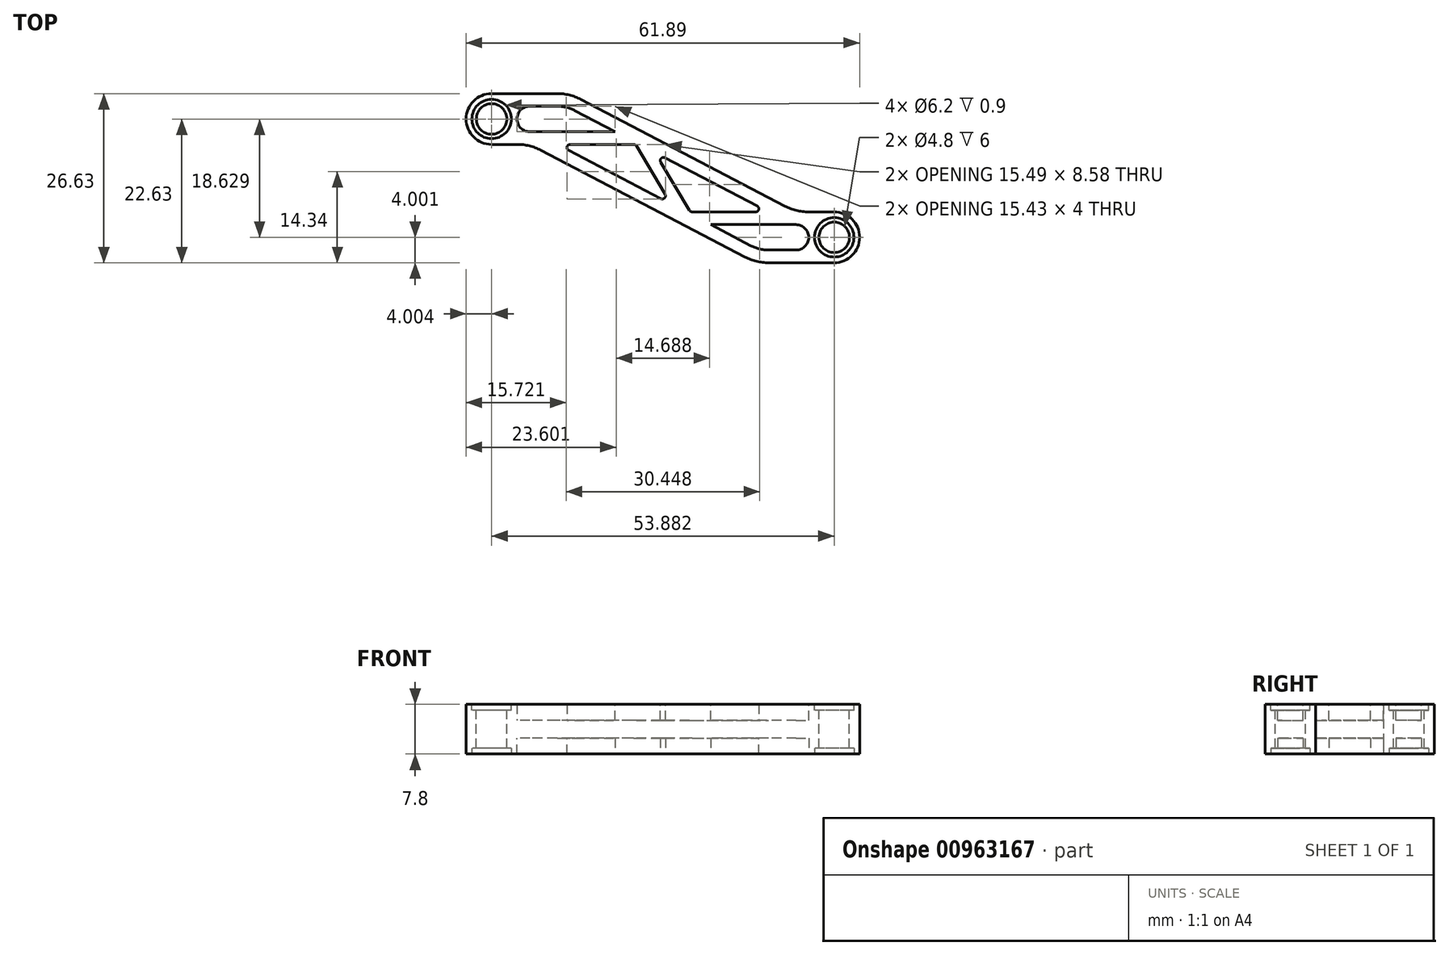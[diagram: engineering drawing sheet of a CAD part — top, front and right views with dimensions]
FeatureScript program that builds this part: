
annotation { "Feature Type Name" : "Feature", "Feature Type Description" : "" }
export const myFeature = defineFeature(function(context is Context, id is Id, definition is map)
    precondition{}
    {
        {
            var Q0;
            Q0=qCreatedBy(makeId("Top.planeOp"),FACE);
            var sketch = newSketch(context, id + "F0", { "sketchPlane" : qUnion([Q0])});
            skLineSegment(sketch, "E0", {"start": v(-26.52, 8) * mm, "end": v(-10.24, 8) * mm});
            skLineSegment(sketch, "E1", {"start": v(-10.24, 8) * mm, "end": v(25.37, -10.63) * mm});
            skLineSegment(sketch, "E2", {"start": v(25.37, -10.63) * mm, "end": v(35.37, -10.63) * mm});
            skLineSegment(sketch, "E3", {"start": v(35.37, -10.63) * mm, "end": v(35.37, -18.63) * mm});
            skLineSegment(sketch, "E4", {"start": v(35.37, -18.63) * mm, "end": v(19.09, -18.63) * mm});
            skLineSegment(sketch, "E5", {"start": v(19.09, -18.63) * mm, "end": v(-16.52, 0) * mm});
            skLineSegment(sketch, "E6", {"start": v(-16.52, 0) * mm, "end": v(-26.52, 0) * mm});
            skLineSegment(sketch, "E7", {"start": v(-26.52, 0) * mm, "end": v(-26.52, 8) * mm});
            skSolve(sketch);
        }
        {
            var Q0;
            Q0 = qSketchRegion(id + "F0", true);
            extrude(context, id + "F1", {"entities" : qUnion([Q0]), "depth" : 3.9 * mm, "offsetDistance" : 25 * mm});
        }
        {
            var Q0;
            Q0=makeQuery(id+"F1.opExtrude","CAP_FACE",FACE,{"disambiguationData":[OSD([sQuery(id+"F0.wireOp",EDGE,"E0"),sQuery(id+"F0.wireOp",EDGE,"E1"),sQuery(id+"F0.wireOp",EDGE,"E2"),sQuery(id+"F0.wireOp",EDGE,"E3"),sQuery(id+"F0.wireOp",EDGE,"E4"),sQuery(id+"F0.wireOp",EDGE,"E5"),sQuery(id+"F0.wireOp",EDGE,"E6"),sQuery(id+"F0.wireOp",EDGE,"E7")])],"isStart":false});
            var sketch = newSketch(context, id + "F2", { "sketchPlane" : qUnion([Q0])});
            skLineSegment(sketch, "E8", {"start": v(-10.73, 6) * mm, "end": v(24.87, -12.63) * mm});
            skLineSegment(sketch, "E9", {"start": v(19.58, -16.63) * mm, "end": v(-16.02, 2) * mm});
            skLineSegment(sketch, "E10", {"start": v(19.09, -18.63) * mm, "end": v(25.37, -10.63) * mm, "construction": true});
            skLineSegment(sketch, "E11", {"start": v(-16.52, 0) * mm, "end": v(-10.24, 8) * mm, "construction": true});
            skLineSegment(sketch, "E12.bottom", {"start": v(27.37, -16.63) * mm, "end": v(19.58, -16.63) * mm});
            skLineSegment(sketch, "E12.top", {"start": v(27.37, -12.63) * mm, "end": v(24.87, -12.63) * mm});
            skLineSegment(sketch, "E12.left", {"start": v(27.37, -16.63) * mm, "end": v(27.37, -12.63) * mm});
            skLineSegment(sketch, "E13.bottom", {"start": v(-16.02, 2) * mm, "end": v(-18.52, 2) * mm});
            skLineSegment(sketch, "E13.top", {"start": v(-10.73, 6) * mm, "end": v(-18.52, 6) * mm});
            skLineSegment(sketch, "E13.right", {"start": v(-18.52, 2) * mm, "end": v(-18.52, 6) * mm});
            skSolve(sketch);
        }
        {
            var Q0;
            Q0=makeQuery(id+"F2.imprint","IMPRINT",FACE,{"disambiguationData":[TD([[makeQuery(id+"F2.imprint","IMPRINT",EDGE,{"derivedFrom":sQuery(id+"F2.wireOp",EDGE,"E8")}),-1.0]])]});
            extrude(context, id + "F3", {"entities" : qUnion([Q0]), "operationType" : NewBodyOperationType.REMOVE, "oppositeDirection" : true, "depth" : (4 - 1.5) * mm, "offsetDistance" : 25 * mm});
        }
        {
            var Q0;
            Q0=makeQuery(id+"F1.opExtrude","CAP_FACE",FACE,{"disambiguationData":[OSD([sQuery(id+"F0.wireOp",EDGE,"E0"),sQuery(id+"F0.wireOp",EDGE,"E1"),sQuery(id+"F0.wireOp",EDGE,"E2"),sQuery(id+"F0.wireOp",EDGE,"E3"),sQuery(id+"F0.wireOp",EDGE,"E4"),sQuery(id+"F0.wireOp",EDGE,"E5"),sQuery(id+"F0.wireOp",EDGE,"E6"),sQuery(id+"F0.wireOp",EDGE,"E7")])],"isStart":false});
            var sketch = newSketch(context, id + "F4", { "sketchPlane" : qUnion([Q0])});
            skLineSegment(sketch, "E14", {"start": v(24.87, -12.63) * mm, "end": v(11.93, -12.63) * mm});
            skLineSegment(sketch, "E15", {"start": v(-16.02, 2) * mm, "end": v(-3.08, 2) * mm});
            skLineSegment(sketch, "E16", {"start": v(21.05, -10.63) * mm, "end": v(8.76, -10.63) * mm});
            skLineSegment(sketch, "E17", {"start": v(-12.2, 0) * mm, "end": v(0.74, 0) * mm});
            skLineSegment(sketch, "E18", {"start": v(5.67, -9.35) * mm, "end": v(-0.2, 0.5) * mm});
            skLineSegment(sketch, "E19", {"start": v(11.93, -12.63) * mm, "end": v(5.67, -9.35) * mm});
            skLineSegment(sketch, "E20", {"start": v(-3.08, 2) * mm, "end": v(3.19, -1.28) * mm});
            skLineSegment(sketch, "E21", {"start": v(-12.2, 0) * mm, "end": v(-16.02, 2) * mm});
            skLineSegment(sketch, "E22", {"start": v(24.87, -12.63) * mm, "end": v(21.05, -10.63) * mm});
            skLineSegment(sketch, "E23.trimOffspring", {"start": v(3.19, -1.28) * mm, "end": v(8.76, -10.63) * mm});
            skSolve(sketch);
        }
        {
            var Q0;
            Q0=makeQuery(id+"F4.imprint","IMPRINT",FACE,{"disambiguationData":[TD([[makeQuery(id+"F4.imprint","IMPRINT",EDGE,{"derivedFrom":sQuery(id+"F4.wireOp",EDGE,"E14")}),-1.0]])]});
            var Q1;
            {var subQ1=sQuery(id+"F4.wireOp",EDGE,"E15");Q1=makeQuery(id+"F4.imprint","IMPRINT",FACE,{"disambiguationData":[TD([[makeQuery(id+"F4.imprint","IMPRINT",EDGE,{"derivedFrom":subQ1}),-1.0]])]});}
            var Q2;
            {var subQ0=sQuery(id+"F4.wireOp",EDGE,"E20");var subQ1=sQuery(id+"F4.wireOp",EDGE,"E17");var subQ2=makeQuery(id+"F4.imprint","INTERSECT",VERTEX,{"derivedFrom":[subQ1,subQ0]});Q2=makeQuery(id+"F4.imprint","IMPRINT",FACE,{"disambiguationData":[TD([[makeQuery(id+"F4.imprint","IMPRINT",EDGE,{"disambiguationData":[TD([[subQ2,1.0]])],"derivedFrom":subQ1}),1.0]])]});}
            var Q3;
            Q3=makeQuery(id+"F3.boolean.opBoolean","COPY",FACE,{"derivedFrom":makeQuery(id+"F3.opExtrude","CAP_FACE",FACE,{"disambiguationData":[OSD([sQuery(id+"F2.wireOp",EDGE,"E8"),sQuery(id+"F2.wireOp",EDGE,"E9"),sQuery(id+"F2.wireOp",EDGE,"E12.bottom"),sQuery(id+"F2.wireOp",EDGE,"E12.top"),sQuery(id+"F2.wireOp",EDGE,"E12.left"),sQuery(id+"F2.wireOp",EDGE,"E13.bottom"),sQuery(id+"F2.wireOp",EDGE,"E13.top"),sQuery(id+"F2.wireOp",EDGE,"E13.right")])],"isStart":false})});
            extrude(context, id + "F5", {"entities" : qUnion([Q0, Q1, Q2]), "operationType" : NewBodyOperationType.ADD, "endBound" : BoundingType.UP_TO_SURFACE, "oppositeDirection" : true, "depth" : 25 * mm, "endBoundEntityFace" : qUnion([Q3]), "offsetDistance" : 25 * mm});
        }
        {
            var Q0;
            Q0=makeQuery(id+"F1.opExtrude","SWEPT_EDGE",EDGE,{"disambiguationData":[OSD([sQuery(id+"F0.wireOp",EDGE,"E0"),sQuery(id+"F0.wireOp",EDGE,"E1")])]});
            var Q1;
            Q1=makeQuery(id+"F1.opExtrude","SWEPT_EDGE",EDGE,{"disambiguationData":[OSD([sQuery(id+"F0.wireOp",EDGE,"E1"),sQuery(id+"F0.wireOp",EDGE,"E2")])]});
            var Q2;
            Q2=makeQuery(id+"F1.opExtrude","SWEPT_EDGE",EDGE,{"disambiguationData":[OSD([sQuery(id+"F0.wireOp",EDGE,"E4"),sQuery(id+"F0.wireOp",EDGE,"E5")])]});
            var Q3;
            Q3=makeQuery(id+"F1.opExtrude","SWEPT_EDGE",EDGE,{"disambiguationData":[OSD([sQuery(id+"F0.wireOp",EDGE,"E5"),sQuery(id+"F0.wireOp",EDGE,"E6")])]});
            fillet(context, id + "F6", {"entities" : qUnion([Q0, Q1, Q2, Q3]), "radius" : 8 * mm, "tangentPropagation" : true, "allowEdgeOverflow" : false});
        }
        {
            var Q0;
            Q0=makeQuery(id+"F1.opExtrude","SWEPT_EDGE",EDGE,{"disambiguationData":[OSD([sQuery(id+"F0.wireOp",EDGE,"E0"),sQuery(id+"F0.wireOp",EDGE,"E7")])]});
            var Q1;
            Q1=makeQuery(id+"F1.opExtrude","SWEPT_EDGE",EDGE,{"disambiguationData":[OSD([sQuery(id+"F0.wireOp",EDGE,"E6"),sQuery(id+"F0.wireOp",EDGE,"E7")])]});
            var Q2;
            Q2=makeQuery(id+"F1.opExtrude","SWEPT_EDGE",EDGE,{"disambiguationData":[OSD([sQuery(id+"F0.wireOp",EDGE,"E2"),sQuery(id+"F0.wireOp",EDGE,"E3")])]});
            var Q3;
            Q3=makeQuery(id+"F1.opExtrude","SWEPT_EDGE",EDGE,{"disambiguationData":[OSD([sQuery(id+"F0.wireOp",EDGE,"E3"),sQuery(id+"F0.wireOp",EDGE,"E4")])]});
            fillet(context, id + "F7", {"entities" : qUnion([Q0, Q1, Q2, Q3]), "radius" : 4 * mm, "tangentPropagation" : true, "allowEdgeOverflow" : false});
        }
        {
            var Q0;
            Q0=makeQuery(id+"F1.opExtrude","CAP_FACE",FACE,{"disambiguationData":[OSD([sQuery(id+"F0.wireOp",EDGE,"E0"),sQuery(id+"F0.wireOp",EDGE,"E1"),sQuery(id+"F0.wireOp",EDGE,"E2"),sQuery(id+"F0.wireOp",EDGE,"E3"),sQuery(id+"F0.wireOp",EDGE,"E4"),sQuery(id+"F0.wireOp",EDGE,"E5"),sQuery(id+"F0.wireOp",EDGE,"E6"),sQuery(id+"F0.wireOp",EDGE,"E7")])],"isStart":false});
            var sketch = newSketch(context, id + "F8", { "sketchPlane" : qUnion([Q0])});
            skCircle(sketch, "E24", {"center": v(-22.52, 4) * mm, "radius": 3.1 * mm});
            skCircle(sketch, "E25", {"center": v(-22.52, 4) * mm, "radius": 2.4 * mm});
            skCircle(sketch, "E26", {"center": v(31.37, -14.63) * mm, "radius": 3.1 * mm});
            skCircle(sketch, "E27", {"center": v(31.37, -14.63) * mm, "radius": 2.4 * mm});
            skSolve(sketch);
        }
        {
            var Q0;
            Q0=makeQuery(id+"F8.imprint","IMPRINT",FACE,{"disambiguationData":[TD([[makeQuery(id+"F8.imprint","IMPRINT",EDGE,{"derivedFrom":sQuery(id+"F8.wireOp",EDGE,"E25")}),1.0]])]});
            var Q1;
            Q1=makeQuery(id+"F8.imprint","IMPRINT",FACE,{"disambiguationData":[TD([[makeQuery(id+"F8.imprint","IMPRINT",EDGE,{"derivedFrom":sQuery(id+"F8.wireOp",EDGE,"E27")}),1.0]])]});
            extrude(context, id + "F9", {"entities" : qUnion([Q0, Q1]), "operationType" : NewBodyOperationType.REMOVE, "endBound" : BoundingType.THROUGH_ALL, "oppositeDirection" : true, "depth" : 25 * mm, "offsetDistance" : 25 * mm});
        }
        {
            var Q0;
            Q0=makeQuery(id+"F8.imprint","IMPRINT",FACE,{"disambiguationData":[TD([[makeQuery(id+"F8.imprint","IMPRINT",EDGE,{"derivedFrom":sQuery(id+"F8.wireOp",EDGE,"E24")}),1.0]])]});
            var Q1;
            Q1=makeQuery(id+"F8.imprint","IMPRINT",FACE,{"disambiguationData":[TD([[makeQuery(id+"F8.imprint","IMPRINT",EDGE,{"derivedFrom":sQuery(id+"F8.wireOp",EDGE,"E26")}),1.0]])]});
            extrude(context, id + "F10", {"entities" : qUnion([Q0, Q1]), "operationType" : NewBodyOperationType.REMOVE, "oppositeDirection" : true, "depth" : .9 * mm, "offsetDistance" : 25 * mm});
        }
        {
            var Q0;
            Q0=makeQuery(id+"F1.opExtrude","SWEPT_BODY",BODY,{"disambiguationData":[OSD([sQuery(id+"F0.wireOp",EDGE,"E0"),sQuery(id+"F0.wireOp",EDGE,"E1"),sQuery(id+"F0.wireOp",EDGE,"E2"),sQuery(id+"F0.wireOp",EDGE,"E3"),sQuery(id+"F0.wireOp",EDGE,"E4"),sQuery(id+"F0.wireOp",EDGE,"E5"),sQuery(id+"F0.wireOp",EDGE,"E6"),sQuery(id+"F0.wireOp",EDGE,"E7")])]});
            var Q1;
            Q1=makeQuery(id+"F1.opExtrude","CAP_FACE",FACE,{"disambiguationData":[OSD([sQuery(id+"F0.wireOp",EDGE,"E0"),sQuery(id+"F0.wireOp",EDGE,"E1"),sQuery(id+"F0.wireOp",EDGE,"E2"),sQuery(id+"F0.wireOp",EDGE,"E3"),sQuery(id+"F0.wireOp",EDGE,"E4"),sQuery(id+"F0.wireOp",EDGE,"E5"),sQuery(id+"F0.wireOp",EDGE,"E6"),sQuery(id+"F0.wireOp",EDGE,"E7")])],"isStart":true});
            mirror(context, id + "F11", {"operationType" : NewBodyOperationType.ADD, "entities" : qUnion([Q0]), "mirrorPlane" : qUnion([Q1])});
        }
        {
            var Q0;
            Q0=makeQuery(id+"F3.boolean.opBoolean","COPY",EDGE,{"derivedFrom":makeQuery(id+"F3.opExtrude","SWEPT_EDGE",EDGE,{"disambiguationData":[OSD([sQuery(id+"F2.wireOp",EDGE,"E12.bottom"),sQuery(id+"F2.wireOp",EDGE,"E12.left")])]})});
            var Q1;
            Q1=makeQuery(id+"F3.boolean.opBoolean","COPY",EDGE,{"derivedFrom":makeQuery(id+"F3.opExtrude","SWEPT_EDGE",EDGE,{"disambiguationData":[OSD([sQuery(id+"F2.wireOp",EDGE,"E12.top"),sQuery(id+"F2.wireOp",EDGE,"E12.left")])]})});
            var Q2;
            Q2=makeQuery(id+"F3.boolean.opBoolean","COPY",EDGE,{"derivedFrom":makeQuery(id+"F3.opExtrude","SWEPT_EDGE",EDGE,{"disambiguationData":[OSD([sQuery(id+"F2.wireOp",EDGE,"E13.bottom"),sQuery(id+"F2.wireOp",EDGE,"E13.right")])]})});
            var Q3;
            Q3=makeQuery(id+"F3.boolean.opBoolean","COPY",EDGE,{"derivedFrom":makeQuery(id+"F3.opExtrude","SWEPT_EDGE",EDGE,{"disambiguationData":[OSD([sQuery(id+"F2.wireOp",EDGE,"E13.top"),sQuery(id+"F2.wireOp",EDGE,"E13.right")])]})});
            var Q4;
            Q4=makeQuery(id+"F11.opPattern","COPY",EDGE,{"derivedFrom":makeQuery(id+"F3.boolean.opBoolean","COPY",EDGE,{"derivedFrom":makeQuery(id+"F3.opExtrude","SWEPT_EDGE",EDGE,{"disambiguationData":[OSD([sQuery(id+"F2.wireOp",EDGE,"E13.bottom"),sQuery(id+"F2.wireOp",EDGE,"E13.right")])]})}),"instanceName":"1"});
            var Q5;
            Q5=makeQuery(id+"F11.opPattern","COPY",EDGE,{"derivedFrom":makeQuery(id+"F3.boolean.opBoolean","COPY",EDGE,{"derivedFrom":makeQuery(id+"F3.opExtrude","SWEPT_EDGE",EDGE,{"disambiguationData":[OSD([sQuery(id+"F2.wireOp",EDGE,"E13.top"),sQuery(id+"F2.wireOp",EDGE,"E13.right")])]})}),"instanceName":"1"});
            var Q6;
            Q6=makeQuery(id+"F11.opPattern","COPY",EDGE,{"derivedFrom":makeQuery(id+"F3.boolean.opBoolean","COPY",EDGE,{"derivedFrom":makeQuery(id+"F3.opExtrude","SWEPT_EDGE",EDGE,{"disambiguationData":[OSD([sQuery(id+"F2.wireOp",EDGE,"E12.bottom"),sQuery(id+"F2.wireOp",EDGE,"E12.left")])]})}),"instanceName":"1"});
            var Q7;
            Q7=makeQuery(id+"F11.opPattern","COPY",EDGE,{"derivedFrom":makeQuery(id+"F3.boolean.opBoolean","COPY",EDGE,{"derivedFrom":makeQuery(id+"F3.opExtrude","SWEPT_EDGE",EDGE,{"disambiguationData":[OSD([sQuery(id+"F2.wireOp",EDGE,"E12.top"),sQuery(id+"F2.wireOp",EDGE,"E12.left")])]})}),"instanceName":"1"});
            fillet(context, id + "F12", {"entities" : qUnion([Q0, Q1, Q2, Q3, Q4, Q5, Q6, Q7]), "radius" : 2 * mm, "tangentPropagation" : true, "allowEdgeOverflow" : false});
        }
        {
            var Q0;
            Q0=makeQuery(id+"F11.opPattern","COPY",EDGE,{"derivedFrom":makeQuery(id+"F3.boolean.opBoolean","COPY",EDGE,{"derivedFrom":makeQuery(id+"F3.opExtrude","SWEPT_EDGE",EDGE,{"disambiguationData":[OSD([sQuery(id+"F2.wireOp",EDGE,"E9"),sQuery(id+"F2.wireOp",EDGE,"E12.bottom")])]})}),"instanceName":"1"});
            var Q1;
            Q1=makeQuery(id+"F11.opPattern","COPY",EDGE,{"derivedFrom":makeQuery(id+"F3.boolean.opBoolean","COPY",EDGE,{"derivedFrom":makeQuery(id+"F3.opExtrude","SWEPT_EDGE",EDGE,{"disambiguationData":[OSD([sQuery(id+"F2.wireOp",EDGE,"E8"),sQuery(id+"F2.wireOp",EDGE,"E13.top")])]})}),"instanceName":"1"});
            var Q2;
            Q2=makeQuery(id+"F3.boolean.opBoolean","COPY",EDGE,{"derivedFrom":makeQuery(id+"F3.opExtrude","SWEPT_EDGE",EDGE,{"disambiguationData":[OSD([sQuery(id+"F2.wireOp",EDGE,"E8"),sQuery(id+"F2.wireOp",EDGE,"E13.top")])]})});
            var Q3;
            Q3=makeQuery(id+"F3.boolean.opBoolean","COPY",EDGE,{"derivedFrom":makeQuery(id+"F3.opExtrude","SWEPT_EDGE",EDGE,{"disambiguationData":[OSD([sQuery(id+"F2.wireOp",EDGE,"E9"),sQuery(id+"F2.wireOp",EDGE,"E12.bottom")])]})});
            fillet(context, id + "F13", {"entities" : qUnion([Q0, Q1, Q2, Q3]), "radius" : 6 * mm, "tangentPropagation" : true, "allowEdgeOverflow" : false});
        }
        {
            var Q0;
            Q0=makeQuery(id+"F5.opExtrude","SWEPT_EDGE",EDGE,{"disambiguationData":[OSD([sQuery(id+"F4.wireOp",EDGE,"E16"),sQuery(id+"F4.wireOp",EDGE,"E23.trimOffspring")])]});
            var Q1;
            Q1=makeQuery(id+"F5.opExtrude","SWEPT_EDGE",EDGE,{"disambiguationData":[OSD([sQuery(id+"F2.wireOp",EDGE,"E8"),sQuery(id+"F4.wireOp",EDGE,"E16"),sQuery(id+"F4.wireOp",EDGE,"E22")])]});
            var Q2;
            Q2=makeQuery(id+"F5.opExtrude","SWEPT_EDGE",EDGE,{"disambiguationData":[OSD([sQuery(id+"F2.wireOp",EDGE,"E8"),sQuery(id+"F4.wireOp",EDGE,"E20"),sQuery(id+"F4.wireOp",EDGE,"E23.trimOffspring")])]});
            var Q3;
            Q3=makeQuery(id+"F5.opExtrude","SWEPT_EDGE",EDGE,{"disambiguationData":[OSD([sQuery(id+"F2.wireOp",EDGE,"E9"),sQuery(id+"F4.wireOp",EDGE,"E14"),sQuery(id+"F4.wireOp",EDGE,"E19")])]});
            var Q4;
            Q4=makeQuery(id+"F5.opExtrude","SWEPT_EDGE",EDGE,{"disambiguationData":[OSD([sQuery(id+"F2.wireOp",EDGE,"E9"),sQuery(id+"F4.wireOp",EDGE,"E17"),sQuery(id+"F4.wireOp",EDGE,"E21")])]});
            var Q5;
            Q5=makeQuery(id+"F5.opExtrude","SWEPT_EDGE",EDGE,{"disambiguationData":[OSD([sQuery(id+"F4.wireOp",EDGE,"E17"),sQuery(id+"F4.wireOp",EDGE,"E18")])]});
            var Q6;
            Q6=makeQuery(id+"F5.opExtrude","SWEPT_EDGE",EDGE,{"disambiguationData":[OSD([sQuery(id+"F2.wireOp",EDGE,"E9"),sQuery(id+"F4.wireOp",EDGE,"E18"),sQuery(id+"F4.wireOp",EDGE,"E19")])]});
            var Q7;
            Q7=makeQuery(id+"F5.opExtrude","SWEPT_EDGE",EDGE,{"disambiguationData":[OSD([sQuery(id+"F2.wireOp",EDGE,"E8"),sQuery(id+"F4.wireOp",EDGE,"E15"),sQuery(id+"F4.wireOp",EDGE,"E20")])]});
            var Q8;
            Q8=makeQuery(id+"F11.opPattern","COPY",EDGE,{"derivedFrom":makeQuery(id+"F5.opExtrude","SWEPT_EDGE",EDGE,{"disambiguationData":[OSD([sQuery(id+"F2.wireOp",EDGE,"E8"),sQuery(id+"F4.wireOp",EDGE,"E15"),sQuery(id+"F4.wireOp",EDGE,"E20")])]}),"instanceName":"1"});
            var Q9;
            Q9=makeQuery(id+"F11.opPattern","COPY",EDGE,{"derivedFrom":makeQuery(id+"F5.opExtrude","SWEPT_EDGE",EDGE,{"disambiguationData":[OSD([sQuery(id+"F2.wireOp",EDGE,"E8"),sQuery(id+"F4.wireOp",EDGE,"E16"),sQuery(id+"F4.wireOp",EDGE,"E22")])]}),"instanceName":"1"});
            var Q10;
            Q10=makeQuery(id+"F11.opPattern","COPY",EDGE,{"derivedFrom":makeQuery(id+"F5.opExtrude","SWEPT_EDGE",EDGE,{"disambiguationData":[OSD([sQuery(id+"F2.wireOp",EDGE,"E9"),sQuery(id+"F4.wireOp",EDGE,"E17"),sQuery(id+"F4.wireOp",EDGE,"E21")])]}),"instanceName":"1"});
            var Q11;
            Q11=makeQuery(id+"F11.opPattern","COPY",EDGE,{"derivedFrom":makeQuery(id+"F5.opExtrude","SWEPT_EDGE",EDGE,{"disambiguationData":[OSD([sQuery(id+"F2.wireOp",EDGE,"E9"),sQuery(id+"F4.wireOp",EDGE,"E14"),sQuery(id+"F4.wireOp",EDGE,"E19")])]}),"instanceName":"1"});
            var Q12;
            Q12=makeQuery(id+"F11.opPattern","COPY",EDGE,{"derivedFrom":makeQuery(id+"F5.opExtrude","SWEPT_EDGE",EDGE,{"disambiguationData":[OSD([sQuery(id+"F4.wireOp",EDGE,"E16"),sQuery(id+"F4.wireOp",EDGE,"E23.trimOffspring")])]}),"instanceName":"1"});
            var Q13;
            Q13=makeQuery(id+"F11.opPattern","COPY",EDGE,{"derivedFrom":makeQuery(id+"F5.opExtrude","SWEPT_EDGE",EDGE,{"disambiguationData":[OSD([sQuery(id+"F2.wireOp",EDGE,"E8"),sQuery(id+"F4.wireOp",EDGE,"E20"),sQuery(id+"F4.wireOp",EDGE,"E23.trimOffspring")])]}),"instanceName":"1"});
            var Q14;
            Q14=makeQuery(id+"F11.opPattern","COPY",EDGE,{"derivedFrom":makeQuery(id+"F5.opExtrude","SWEPT_EDGE",EDGE,{"disambiguationData":[OSD([sQuery(id+"F4.wireOp",EDGE,"E17"),sQuery(id+"F4.wireOp",EDGE,"E18")])]}),"instanceName":"1"});
            var Q15;
            Q15=makeQuery(id+"F11.opPattern","COPY",EDGE,{"derivedFrom":makeQuery(id+"F5.opExtrude","SWEPT_EDGE",EDGE,{"disambiguationData":[OSD([sQuery(id+"F2.wireOp",EDGE,"E9"),sQuery(id+"F4.wireOp",EDGE,"E18"),sQuery(id+"F4.wireOp",EDGE,"E19")])]}),"instanceName":"1"});
            fillet(context, id + "F14", {"entities" : qUnion([Q0, Q1, Q2, Q3, Q4, Q5, Q6, Q7, Q8, Q9, Q10, Q11, Q12, Q13, Q14, Q15]), "radius" : .5 * mm, "tangentPropagation" : true, "allowEdgeOverflow" : false});
        }
    });
